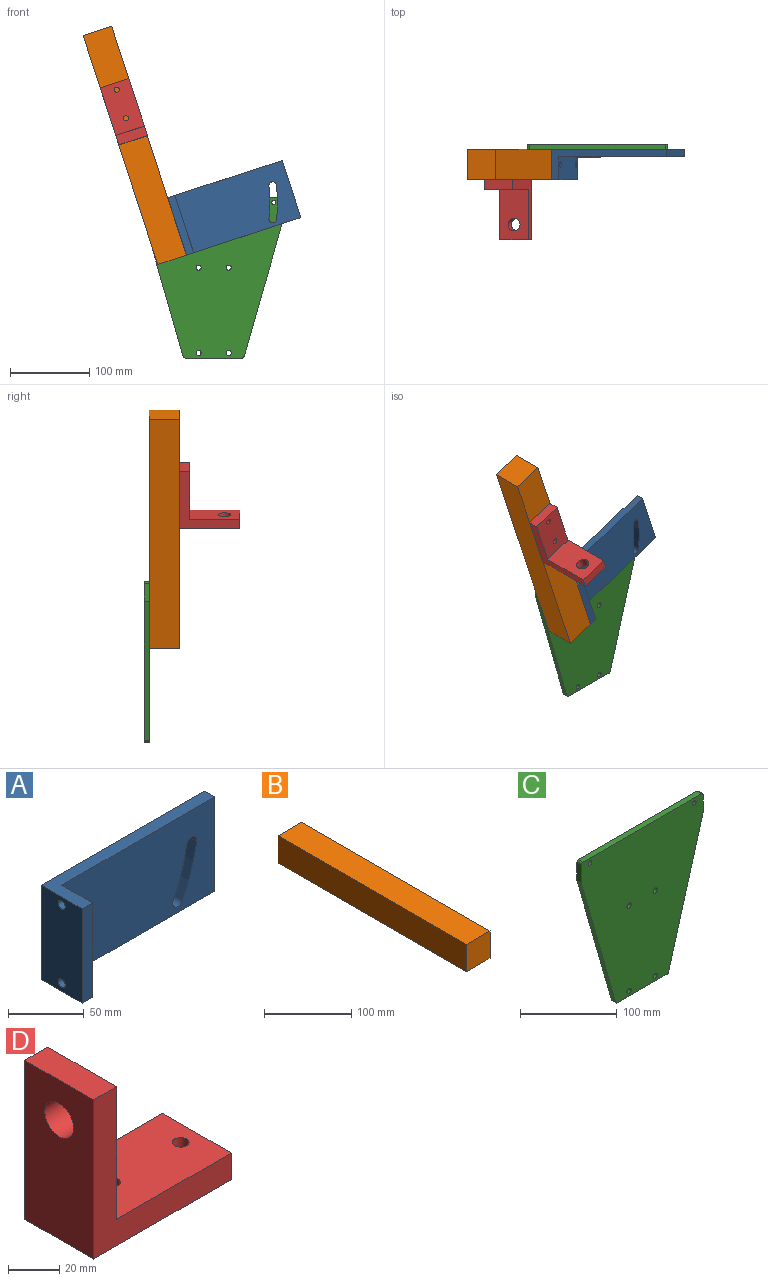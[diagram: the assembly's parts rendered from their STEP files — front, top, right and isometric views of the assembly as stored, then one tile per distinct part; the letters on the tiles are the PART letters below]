
ASSEMBLY  parts=4 mates=6
PART A: 14 faces, bbox 152.4x38.1x76.2 mm
  f0: cylinder r=147.64mm len=39.08mm, axis (0,1,0), area 392.7mm2, adj f1,f7,f8,f9
  f1: cylinder r=4.76mm len=9.53mm, axis (0,1,0), area 142.5mm2, adj f0,f2,f8,f9
  f2: cylinder r=157.16mm len=41.6mm, axis (0,1,0), area 418mm2, adj f1,f7,f8,f9
  f3: plane 152.4x38.1mm, normal (0,0,1), area 1723.8mm2, adj f4,f6,f8,f9,f10,f11
  f4: plane 76.2x38.1mm, normal (-1,0,0), area 2836.3mm2, adj f3,f5,f9,f11,f12,f13
  f5: plane 152.4x38.1mm, normal (0,0,-1), area 1723.8mm2, adj f4,f6,f8,f9,f10,f11
  f6: plane 76.2x9.53mm, normal (1,0,0), area 725.8mm2, adj f3,f5,f8,f9
  f7: cylinder r=4.76mm len=9.53mm, axis (0,1,0), area 142.5mm2, adj f0,f2,f8,f9
  f8: plane 142.88x76.2mm, normal (0,-1,0), area 10410.5mm2, adj f0,f1,f2,f3,f5,f6,f7,f10
  f9: plane 152.4x76.2mm, normal (0,1,0), area 11136.3mm2, adj f0,f1,f2,f3,f4,f5,f6,f7
  f10: plane 76.2x28.58mm, normal (1,0,0), area 2110.5mm2, adj f3,f5,f8,f11,f12,f13
  f11: plane 76.2x9.53mm, normal (0,-1,0), area 725.8mm2, adj f3,f4,f5,f10
  f12: cylinder r=3.26mm len=9.53mm, axis (-1,0,0), area 195.3mm2, adj f4,f10
  f13: cylinder r=3.26mm len=9.53mm, axis (-1,0,0), area 195.3mm2, adj f4,f10
PART B: 6 faces, bbox 38.1x304.8x38.1 mm
  f0: plane 304.8x38.1mm, normal (0,0,1), area 11612.9mm2, adj f1,f3,f4,f5
  f1: plane 304.8x38.1mm, normal (-1,0,0), area 11612.9mm2, adj f0,f2,f4,f5
  f2: plane 304.8x38.1mm, normal (0,0,-1), area 11612.9mm2, adj f1,f3,f4,f5
  f3: plane 304.8x38.1mm, normal (1,0,0), area 11612.9mm2, adj f0,f2,f4,f5
  f4: plane 38.1x38.1mm, normal (0,-1,0), area 1451.6mm2, adj f0,f1,f2,f3
  f5: plane 38.1x38.1mm, normal (0,1,0), area 1451.6mm2, adj f0,f1,f2,f3
PART C: 20 faces, bbox 177.8x6.4x203.2 mm
  f0: cylinder r=2.54mm len=6.35mm, axis (0,1,0), area 20.8mm2, adj f1,f17,f18,f19
  f1: plane 72.37x6.35mm, normal (0,0,-1), area 459.5mm2, adj f0,f2,f18,f19
  f2: cylinder r=2.54mm len=6.35mm, axis (0,1,0), area 20.8mm2, adj f1,f3,f18,f19
  f3: plane 175.62x50.18mm, normal (0.96,0,-0.27), area 1159.8mm2, adj f2,f4,f18,f19
  f4: cylinder r=2.54mm len=6.35mm, axis (0,1,0), area 4.5mm2, adj f3,f5,f18,f19
  f5: plane 22.5x6.35mm, normal (1,0,0), area 142.9mm2, adj f4,f6,f18,f19
  f6: cylinder r=2.54mm len=6.35mm, axis (0,1,0), area 25.3mm2, adj f5,f7,f18,f19
  f7: plane 172.72x6.35mm, normal (0,0,1), area 1096.8mm2, adj f6,f8,f18,f19
  f8: cylinder r=2.54mm len=6.35mm, axis (0,1,0), area 25.3mm2, adj f7,f9,f18,f19
  f9: plane 22.5x6.35mm, normal (-1,0,0), area 142.9mm2, adj f8,f10,f18,f19
  f10: cylinder r=2.54mm len=6.35mm, axis (0,1,0), area 4.5mm2, adj f9,f17,f18,f19
  f11: cylinder r=3.26mm len=6.53mm, axis (0,1,0), area 130.2mm2, adj f18,f19
  f12: cylinder r=3.26mm len=6.53mm, axis (0,1,0), area 130.2mm2, adj f18,f19
  f13: cylinder r=3.26mm len=6.53mm, axis (0,1,0), area 130.2mm2, adj f18,f19
  f14: cylinder r=3.26mm len=6.53mm, axis (0,1,0), area 130.2mm2, adj f18,f19
  f15: cylinder r=2.55mm len=6.35mm, axis (0,1,0), area 101.8mm2, adj f18,f19
  f16: cylinder r=2.55mm len=6.35mm, axis (0,1,0), area 101.8mm2, adj f18,f19
  f17: plane 175.62x50.18mm, normal (-0.96,0,-0.27), area 1159.8mm2, adj f0,f10,f18,f19
  f18: plane 203.2x177.8mm, normal (0,-1,0), area 26917.7mm2, adj f0,f1,f2,f3,f4,f5,f6,f7
  f19: plane 203.2x177.8mm, normal (0,1,0), area 26917.7mm2, adj f0,f1,f2,f3,f4,f5,f6,f7
PART D: 11 faces, bbox 76.2x38.1x76.2 mm
  f0: plane 76.2x76.2mm, normal (0,1,0), area 1774.2mm2, adj f1,f3,f4,f5,f6,f7
  f1: plane 76.2x38.1mm, normal (-1,0,0), area 2705.3mm2, adj f0,f2,f5,f7,f8
  f2: plane 76.2x76.2mm, normal (0,-1,0), area 1774.2mm2, adj f1,f3,f4,f5,f6,f7
  f3: plane 38.1x12.7mm, normal (1,0,0), area 483.9mm2, adj f0,f2,f4,f5
  f4: plane 63.5x38.1mm, normal (0,0,1), area 2352.4mm2, adj f0,f2,f3,f6,f9,f10
  f5: plane 76.2x38.1mm, normal (0,0,-1), area 2836.3mm2, adj f0,f1,f2,f3,f9,f10
  f6: plane 63.5x38.1mm, normal (1,0,0), area 2221.4mm2, adj f0,f2,f4,f7,f8
  f7: plane 38.1x12.7mm, normal (0,0,1), area 483.9mm2, adj f0,f1,f2,f6
  f8: cylinder r=7.94mm len=15.88mm, axis (-1,0,0), area 633.4mm2, adj f1,f6
  f9: cylinder r=3.26mm len=12.7mm, axis (0,0,-1), area 260.4mm2, adj f4,f5
  f10: cylinder r=3.26mm len=12.7mm, axis (0,0,-1), area 260.4mm2, adj f4,f5
PLACE A rot(axis=(0,-1,0),18.1deg) t=(35.55,-6.35,-65.41)mm
PLACE B rot(axis=(-0.98,-0.16,-0.16),91.4deg) t=(-0.68,-44.45,-77.22)mm
PLACE C t=(-18.89,0,7.48)mm fixed
PLACE D rot(axis=(0.46,-0.63,0.63),130.9deg) t=(-13.7,-44.45,85.62)mm
MATE revolute A.f0 <-> C.f15  axis (0,1,0) through (-6.19,-6.35,1.13)mm
MATE planar B.f3 <-> A.f4  axis (0.95,0,0.31) through (-11.7,-25.4,79.48)mm
MATE planar D.f0 <-> B.f1  axis (-0.95,0,-0.31) through (-57.26,-68.12,96.31)mm
MATE planar A.f11 <-> B.f2  axis (0,-1,0) through (28.26,-44.45,-27.71)mm
MATE planar B.f2 <-> D.f5  axis (0,-1,0) through (-29.81,-44.45,73.57)mm
MATE planar B.f5 <-> A.f5  axis (0.31,0,-0.95) through (17.43,-25.4,-71.32)mm
